# Revit family: Gira_542000
name_source: partatom
category: Elektroinstallationen
revit_build: Autodesk Revit 2017 (Build: 20160225_1515(x64)
units: mm (PartAtom-declared; Revit-internal decimal feet)

## family parameters
Basisbauteil = Fläche
Beim Laden mit Abzugskörper schneiden = Nein
Bemaßung runder Anschluss = Durchmesser verwenden
Beschriftungsausrichtung beibehalten = Nein
Gemeinsam genutzt = Nein
Raumberechnungspunkt = Nein
Teiletyp = Normal

## types (1)
- Gira_542000
    BIM = https://media.stage.bim.site
    Beschreibung = WL dimm.act.1g Mini eNet,eNet wireless dimming actuator, 1-gang Mini,20 - 250 W VA,,Features:,Can be set with eNet server::,- Fully encrypted wireless transmission (AES CCM) from eNet Server software version 2.0.,- Operation locks.,- Device software update.,- The eNet wireless dimming actuator enables switching and dimming of various electrical loads.,- Switching and dimming light bulbs, HV halogen lamps, electronic transformers for halogen or LED lamps, dimmable inductive transformers for halogen or LED lamps, HV LED or compact fluorescent lamps.,- Bulb-saving switch-on.,- Switch-on and minimum brightness can be saved for each output.,- Scene operation.,- Status display with LED.,- Status feedback to eNet wireless sensors.,- Short-circuit and excess-temperature protection.,- Automatic or manual setting of dimming process.,Can be set with eNet server::,- Maximum brightness.,- Dimming process.,- Dimming speed.,- Delay time.,- Switch-on off delay.,- Dimming ramp up down.,- Switch-off pre-warning.,- Permanent-on, permanent-off.,- Hotel function.,- Light control.,- Repeater function.,- Localisation of the device.,,Notes :,- Installation in device box, surface-mounted housing, or in an installation adapter.
    Bus connection included = Nein
    Bus system KNX = Nein
    Bus system KNX radio = Nein
    Bus system LON = Nein
    Bus system Powernet = Nein
    Bus system radio frequent = Ja
    Data sheet = https://katalog.gira.de
    Degree of protection (IP) = IP20
    Different phases connectable = Nein
    GTIN = 4010337774143
    HAN = 542000
    Hersteller = Gira
    Local operation/hand operation = Nein
    Model = Dimming actuator
    Modular expandability = Nein
    Mounting method = Flush mounted (plaster)
    Number of outputs = 1
    Other bus systems = None
    Output power [Voltampere] = [250:250]
    Parallel-service possible = Nein
    Power boost suitable = Nein
    Productwebsite = http://katalog.gira.de
    Substation input = Nein
    Suitable for C-load = Nein
    Type of load = Universal
    Typname = WL dimm.act. 1-g Mini 20 - 250 VA Gira eNet
    URL = https://www.gira.de
    Voltage [Volt] = [230:230]
    Vorgabe-Ansicht = 1219 mm
    With LED indication = Nein

## geometry (parser evidence)
native form markers: Sweep x2
no freeform markers — native parametric forms only
